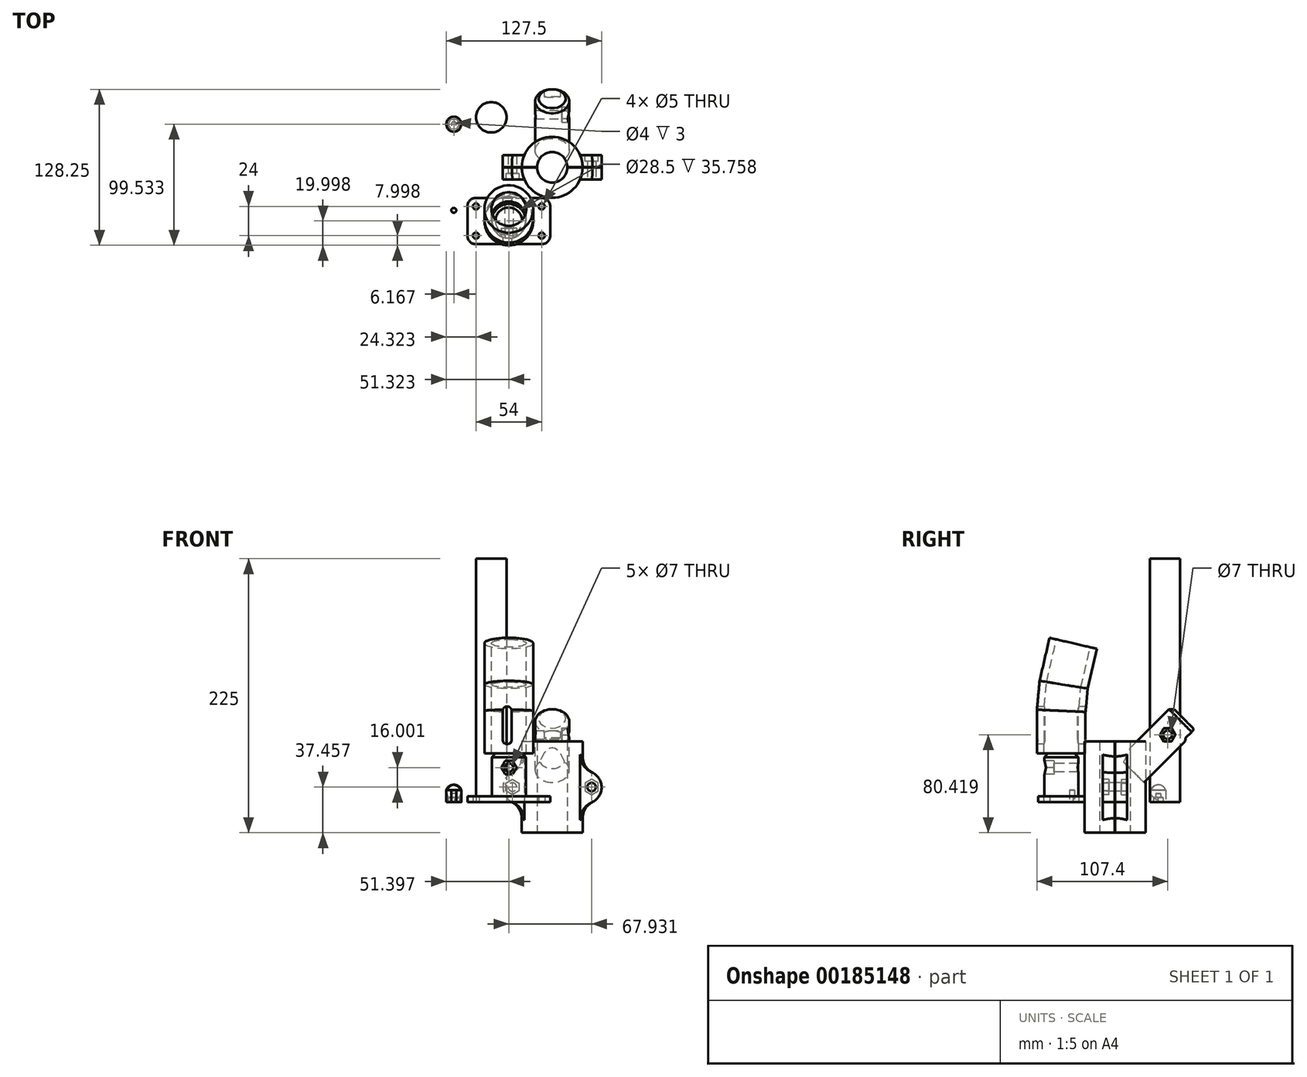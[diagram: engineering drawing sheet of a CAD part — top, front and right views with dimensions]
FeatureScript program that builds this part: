
annotation { "Feature Type Name" : "Feature", "Feature Type Description" : "" }
export const myFeature = defineFeature(function(context is Context, id is Id, definition is map)
    precondition{}
    {
        {
            var Q0;
            Q0=qCreatedBy(makeId("Top.planeOp"),FACE);
            var sketch = newSketch(context, id + "F0", { "sketchPlane" : qUnion([Q0])});
            skCircle(sketch, "E0", {"center": v(0, 0) * mm, "radius": 12.5 * mm});
            skCircle(sketch, "E1", {"center": v(0, 0) * mm, "radius": 25 * mm});
            skSolve(sketch);
        }
        {
            var Q0;
            Q0=makeQuery(id+"F0.imprint","IMPRINT",FACE,{"disambiguationData":[TD([[makeQuery(id+"F0.imprint","IMPRINT",EDGE,{"derivedFrom":sQuery(id+"F0.wireOp",EDGE,"E0")}),-1.0]])]});
            extrude(context, id + "F1", {"entities" : qUnion([Q0]), "depth" : 50 * mm, "symmetric" : true});
        }
        {
            var Q0;
            Q0=qCreatedBy(makeId("Front.planeOp"),FACE);
            var sketch = newSketch(context, id + "F2", { "sketchPlane" : qUnion([Q0])});
            skCircle(sketch, "E2", {"center": v(-26.98, 12.25) * mm, "radius": 13.5 * mm});
            skCircle(sketch, "E3", {"center": v(27.04, 12.25) * mm, "radius": 13.5 * mm});
            skLineSegment(sketch, "E4", {"start": v(27.04, 12.25) * mm, "end": v(-26.98, 12.25) * mm, "construction": true});
            skSolve(sketch);
        }
        {
            var Q0;
            Q0=qSketchRegion(id+"F2",true);
            extrude(context, id + "F3", {"entities" : qUnion([Q0]), "operationType" : NewBodyOperationType.ADD, "depth" : 20 * mm, "symmetric" : true});
        }
        {
            var Q0;
            Q0=makeQuery(id+"F3.opExtrude","CAP_FACE",FACE,{"disambiguationData":[OSD([sQuery(id+"F2.wireOp",EDGE,"E2")])],"isStart":false});
            var sketch = newSketch(context, id + "F4", { "sketchPlane" : qUnion([Q0])});
            skCircle(sketch, "E5", {"center": v(-32.64, 12.46) * mm, "radius": 3.5 * mm});
            skCircle(sketch, "E6", {"center": v(32.37, 12.46) * mm, "radius": 3.5 * mm});
            skLineSegment(sketch, "E7", {"start": v(-40.47, 12.46) * mm, "end": v(40.61, 12.46) * mm, "construction": true});
            skLineSegment(sketch, "E8", {"start": v(32.37, 24.7) * mm, "end": v(32.37, 0) * mm, "construction": true});
            skLineSegment(sketch, "E9", {"start": v(32.37, 0) * mm, "end": v(-32.64, 0) * mm, "construction": true});
            skLineSegment(sketch, "E10", {"start": v(-32.64, 0) * mm, "end": v(-32.64, 24.5) * mm, "construction": true});
            skLineSegment(sketch, "E11", {"start": v(-32.64, 24.5) * mm, "end": v(32.37, 24.7) * mm, "construction": true});
            skSolve(sketch);
        }
        {
            var Q0;
            Q0=qSketchRegion(id+"F4",true);
            extrude(context, id + "F5", {"entities" : qUnion([Q0]), "operationType" : NewBodyOperationType.REMOVE, "oppositeDirection" : true, "depth" : 25 * mm});
        }
        {
            var Q0;
            Q0=makeQuery(id+"F3.opExtrude","CAP_FACE",FACE,{"disambiguationData":[OSD([sQuery(id+"F2.wireOp",EDGE,"E2")])],"isStart":false});
            var sketch = newSketch(context, id + "F6", { "sketchPlane" : qUnion([Q0])});
            skCircle(sketch, "E12.cCircle", {"center": v(-32.64, 12.46) * mm, "radius": 5.5 * mm, "construction": true});
            skLineSegment(sketch, "E12.0", {"start": v(-27.14, 15.63) * mm, "end": v(-27.14, 9.28) * mm});
            skLineSegment(sketch, "E12.1", {"start": v(-27.14, 9.28) * mm, "end": v(-32.64, 6.1) * mm});
            skLineSegment(sketch, "E12.2", {"start": v(-32.64, 6.1) * mm, "end": v(-38.14, 9.28) * mm});
            skLineSegment(sketch, "E12.3", {"start": v(-38.14, 9.28) * mm, "end": v(-38.14, 15.63) * mm});
            skLineSegment(sketch, "E12.4", {"start": v(-38.14, 15.63) * mm, "end": v(-32.64, 18.8) * mm});
            skLineSegment(sketch, "E12.5", {"start": v(-32.64, 18.8) * mm, "end": v(-27.14, 15.63) * mm});
            skPoint(sketch, "E12.0.midPoint", {"position": v(-27.14, 12.46) * mm});
            skLineSegment(sketch, "E13", {"start": v(-38.14, 12.46) * mm, "end": v(-27.14, 12.46) * mm, "construction": true});
            skSolve(sketch);
        }
        {
            var Q0;
            Q0=qSketchRegion(id+"F6",true);
            extrude(context, id + "F7", {"entities" : qUnion([Q0]), "operationType" : NewBodyOperationType.REMOVE, "oppositeDirection" : true, "depth" : 5 * mm});
        }
        {
            var Q0;
            Q0=makeQuery(id+"F3.opExtrude","CAP_FACE",FACE,{"disambiguationData":[OSD([sQuery(id+"F2.wireOp",EDGE,"E3")])],"isStart":true});
            var sketch = newSketch(context, id + "F8", { "sketchPlane" : qUnion([Q0])});
            skCircle(sketch, "E14.cCircle", {"center": v(-32.37, 12.46) * mm, "radius": 5.5 * mm, "construction": true});
            skLineSegment(sketch, "E14.0", {"start": v(-26.87, 15.63) * mm, "end": v(-26.87, 9.28) * mm});
            skLineSegment(sketch, "E14.1", {"start": v(-26.87, 9.28) * mm, "end": v(-32.37, 6.1) * mm});
            skLineSegment(sketch, "E14.2", {"start": v(-32.37, 6.1) * mm, "end": v(-37.87, 9.28) * mm});
            skLineSegment(sketch, "E14.3", {"start": v(-37.87, 9.28) * mm, "end": v(-37.87, 15.63) * mm});
            skLineSegment(sketch, "E14.4", {"start": v(-37.87, 15.63) * mm, "end": v(-32.37, 18.8) * mm});
            skLineSegment(sketch, "E14.5", {"start": v(-32.37, 18.8) * mm, "end": v(-26.87, 15.63) * mm});
            skPoint(sketch, "E14.0.midPoint", {"position": v(-26.87, 12.46) * mm});
            skLineSegment(sketch, "E15", {"start": v(-26.87, 12.46) * mm, "end": v(-37.87, 12.46) * mm, "construction": true});
            skSolve(sketch);
        }
        {
            var Q0;
            Q0=qSketchRegion(id+"F8",true);
            extrude(context, id + "F9", {"entities" : qUnion([Q0]), "operationType" : NewBodyOperationType.REMOVE, "oppositeDirection" : true, "depth" : 5 * mm});
        }
        {
            var Q0;
            {var subQ0=sQuery(id+"F0.wireOp",EDGE,"E0");var subQ1=sQuery(id+"F0.wireOp",EDGE,"E1");Q0=makeQuery(id+"FAVgWfvb4NsKyi1_1.boolean.opBoolean","SPLIT",FACE,{"disambiguationData":[TD([makeQuery(id+"FAVgWfvb4NsKyi1_1.opExtrude","SWEPT_FACE",FACE,{"disambiguationData":[OSD([sQuery(id+"FL5HWG1BF790Trn_1.wireOp",EDGE,"xYHfgR5R-DCME-g4vK-4hEz-Q0mkNuq86y99.top")])]})])],"derivedFrom":makeQuery(id+"F1.opExtrude","CAP_FACE",FACE,{"disambiguationData":[OSD([subQ0,subQ1])],"isStart":false})});}
            extrude(context, id + "F10", {"entities" : qUnion([Q0]), "operationType" : NewBodyOperationType.ADD, "depth" : 25 * mm});
        }
        {
            var Q0;
            Q0=qCreatedBy(makeId("Top.planeOp"),FACE);
            var sketch = newSketch(context, id + "F11", { "sketchPlane" : qUnion([Q0])});
            skLineSegment(sketch, "E16.bottom", {"start": v(-62.64, -25.15) * mm, "end": v(-8.64, -25.15) * mm});
            skLineSegment(sketch, "E16.top", {"start": v(-62.64, -63.15) * mm, "end": v(-8.64, -63.15) * mm});
            skLineSegment(sketch, "E16.left", {"start": v(-69.64, -32.15) * mm, "end": v(-69.64, -56.15) * mm});
            skLineSegment(sketch, "E16.right", {"start": v(-1.64, -32.15) * mm, "end": v(-1.64, -56.15) * mm});
            skCircle(sketch, "E17", {"center": v(-62.64, -32.15) * mm, "radius": 2.5 * mm});
            skCircle(sketch, "E18", {"center": v(-62.64, -56.15) * mm, "radius": 2.5 * mm});
            skCircle(sketch, "E19", {"center": v(-8.64, -32.15) * mm, "radius": 2.5 * mm});
            skCircle(sketch, "E20", {"center": v(-8.64, -56.15) * mm, "radius": 2.5 * mm});
            skLineSegment(sketch, "E21", {"start": v(-62.67, -25.15) * mm, "end": v(-62.64, -32.15) * mm, "construction": true});
            skLineSegment(sketch, "E22", {"start": v(-62.64, -32.15) * mm, "end": v(-69.64, -32.19) * mm, "construction": true});
            skLineSegment(sketch, "E23", {"start": v(-8.64, -56.15) * mm, "end": v(-1.64, -56.15) * mm, "construction": true});
            skLineSegment(sketch, "E24", {"start": v(-8.64, -56.15) * mm, "end": v(-8.64, -63.15) * mm, "construction": true});
            skLineSegment(sketch, "E25.bottom", {"start": v(-62.64, -32.15) * mm, "end": v(-8.64, -32.15) * mm, "construction": true});
            skLineSegment(sketch, "E25.top", {"start": v(-62.64, -56.15) * mm, "end": v(-8.64, -56.15) * mm, "construction": true});
            skLineSegment(sketch, "E25.left", {"start": v(-62.64, -32.15) * mm, "end": v(-62.64, -56.15) * mm, "construction": true});
            skLineSegment(sketch, "E25.right", {"start": v(-8.64, -32.15) * mm, "end": v(-8.64, -56.15) * mm, "construction": true});
            skPoint(sketch, "E26.visualSharp", {"position": v(-69.64, -25.15) * mm});
            skArc(sketch, "E26.filletArc", {"start": v(-62.64, -25.15) * mm, "mid": v(-67.59, -27.2) * mm, "end": v(-69.64, -32.15) * mm});
            skPoint(sketch, "E27.visualSharp", {"position": v(-69.64, -63.15) * mm});
            skArc(sketch, "E27.filletArc", {"start": v(-69.64, -56.15) * mm, "mid": v(-67.59, -61.1) * mm, "end": v(-62.64, -63.15) * mm});
            skPoint(sketch, "E28.visualSharp", {"position": v(-1.64, -63.15) * mm});
            skArc(sketch, "E28.filletArc", {"start": v(-8.64, -63.15) * mm, "mid": v(-3.69, -61.1) * mm, "end": v(-1.64, -56.15) * mm});
            skPoint(sketch, "E29.visualSharp", {"position": v(-1.64, -25.15) * mm});
            skArc(sketch, "E29.filletArc", {"start": v(-1.64, -32.15) * mm, "mid": v(-3.69, -27.2) * mm, "end": v(-8.64, -25.15) * mm});
            skSolve(sketch);
        }
        {
            var Q0;
            Q0=qSketchRegion(id+"F11",true);
            extrude(context, id + "F12", {"entities" : qUnion([Q0]), "depth" : 5 * mm});
        }
        {
            var Q0;
            Q0=makeQuery(id+"F12.opExtrude","CAP_FACE",FACE,{"disambiguationData":[OSD([sQuery(id+"F11.wireOp",EDGE,"E16.bottom"),sQuery(id+"F11.wireOp",EDGE,"E16.top"),sQuery(id+"F11.wireOp",EDGE,"E16.left"),sQuery(id+"F11.wireOp",EDGE,"E16.right"),sQuery(id+"F11.wireOp",EDGE,"E17"),sQuery(id+"F11.wireOp",EDGE,"E18"),sQuery(id+"F11.wireOp",EDGE,"E19"),sQuery(id+"F11.wireOp",EDGE,"E20"),sQuery(id+"F11.wireOp",EDGE,"E26.filletArc"),sQuery(id+"F11.wireOp",EDGE,"E27.filletArc"),sQuery(id+"F11.wireOp",EDGE,"E28.filletArc"),sQuery(id+"F11.wireOp",EDGE,"E29.filletArc")])],"isStart":false});
            var sketch = newSketch(context, id + "F13", { "sketchPlane" : qUnion([Q0])});
            skCircle(sketch, "E30", {"center": v(-35.64, -44.15) * mm, "radius": 14 * mm});
            skLineSegment(sketch, "E31", {"start": v(-69.64, -44.15) * mm, "end": v(-1.64, -44.15) * mm, "construction": true});
            skLineSegment(sketch, "E32", {"start": v(-35.64, -25.15) * mm, "end": v(-35.64, -63.15) * mm, "construction": true});
            skSolve(sketch);
        }
        {
            var Q0;
            Q0=qSketchRegion(id+"F13",true);
            extrude(context, id + "F14", {"entities" : qUnion([Q0]), "operationType" : NewBodyOperationType.ADD, "depth" : 35 * mm});
        }
        {
            var Q0;
            Q0=qCreatedBy(makeId("Top.planeOp"),FACE);
            var sketch = newSketch(context, id + "F15", { "sketchPlane" : qUnion([Q0])});
            skCircle(sketch, "E33", {"center": v(-50.03, 41.05) * mm, "radius": 12.5 * mm});
            skSolve(sketch);
        }
        {
            var Q0;
            Q0=qSketchRegion(id+"F15",true);
            extrude(context, id + "F16", {"entities" : qUnion([Q0]), "depth" : 200 * mm});
        }
        {
            var Q0;
            Q0=makeQuery(id+"F14.opExtrude","CAP_FACE",FACE,{"disambiguationData":[OSD([sQuery(id+"F13.wireOp",EDGE,"E30")])],"isStart":false});
            var sketch = newSketch(context, id + "F17", { "sketchPlane" : qUnion([Q0])});
            skCircle(sketch, "E34", {"center": v(-35.64, -44.15) * mm, "radius": 14.25 * mm});
            skCircle(sketch, "E35", {"center": v(-35.64, -44.15) * mm, "radius": 20 * mm});
            skSolve(sketch);
        }
        {
            var Q0;
            Q0=qCreatedBy(makeId("Right.planeOp"),FACE);
            cPlane(context, id + "F18", {"entities" : qUnion([Q0]), "cplaneType" : CPlaneType.OFFSET, "offset" : 37 * mm, "oppositeDirection" : true, "width" : 150 * mm, "height" : 150 * mm});
        }
        {
            var Q0;
            Q0=qCreatedBy(id+"F18.planeOp",FACE);
            var sketch = newSketch(context, id + "F19", { "sketchPlane" : qUnion([Q0])});
            skLineSegment(sketch, "E36", {"start": v(-44.05, 40.1) * mm, "end": v(-44.05, 75.1) * mm});
            skLineSegment(sketch, "E37", {"start": v(-57.92, 40.1) * mm, "end": v(-30.17, 40.1) * mm, "construction": true});
            skLineSegment(sketch, "E38", {"start": v(-42.05, 96.55) * mm, "end": v(-34.15, 130.64) * mm});
            skLineSegment(sketch, "E39", {"start": v(-42.05, 96.55) * mm, "end": v(-44.05, 75.1) * mm});
            skSolve(sketch);
        }
        {
            var Q0;
            Q0=makeQuery(id+"F17.imprint","IMPRINT",FACE,{"disambiguationData":[TD([[makeQuery(id+"F17.imprint","IMPRINT",EDGE,{"derivedFrom":sQuery(id+"F17.wireOp",EDGE,"E34")}),-1.0]])]});
            var Q1;
            Q1=sQuery(id+"F19.wireOp",EDGE,"E36");
            var Q2;
            Q2=sQuery(id+"F19.wireOp",EDGE,"E39");
            var Q3;
            Q3=sQuery(id+"F19.wireOp",EDGE,"E38");
            sweep(context, id + "F20", {"profiles" : qUnion([Q0]), "path" : qUnion([Q1, Q2, Q3])});
        }
        {
            var Q0;
            Q0=makeQuery(id+"F12.opExtrude","CAP_FACE",FACE,{"disambiguationData":[OSD([sQuery(id+"F11.wireOp",EDGE,"E16.bottom"),sQuery(id+"F11.wireOp",EDGE,"E16.top"),sQuery(id+"F11.wireOp",EDGE,"E16.left"),sQuery(id+"F11.wireOp",EDGE,"E16.right"),sQuery(id+"F11.wireOp",EDGE,"E17"),sQuery(id+"F11.wireOp",EDGE,"E18"),sQuery(id+"F11.wireOp",EDGE,"E19"),sQuery(id+"F11.wireOp",EDGE,"E20"),sQuery(id+"F11.wireOp",EDGE,"E26.filletArc"),sQuery(id+"F11.wireOp",EDGE,"E27.filletArc"),sQuery(id+"F11.wireOp",EDGE,"E28.filletArc"),sQuery(id+"F11.wireOp",EDGE,"E29.filletArc")])],"isStart":true});
            var sketch = newSketch(context, id + "F21", { "sketchPlane" : qUnion([Q0])});
            skCircle(sketch, "E40", {"center": v(-62.64, 56.15) * mm, "radius": 2.5 * mm});
            skCircle(sketch, "E41", {"center": v(-62.64, 56.15) * mm, "radius": 5.5 * mm});
            skSolve(sketch);
        }
        {
            var Q0;
            Q0=makeQuery(id+"F21.imprint","IMPRINT",FACE,{"disambiguationData":[TD([[makeQuery(id+"F21.imprint","IMPRINT",EDGE,{"derivedFrom":sQuery(id+"F21.wireOp",EDGE,"E40")}),-1.0]])]});
            extrude(context, id + "F22", {"entities" : qUnion([Q0]), "depth" : 2.5 * mm});
        }
        {
            var Q0;
            Q0=qCreatedBy(makeId("Top.planeOp"),FACE);
            var sketch = newSketch(context, id + "F23", { "sketchPlane" : qUnion([Q0])});
            skCircle(sketch, "E42", {"center": v(0, 56.93) * mm, "radius": 14 * mm});
            skSolve(sketch);
        }
        {
            var Q0;
            Q0=qSketchRegion(id+"F23",true);
            extrude(context, id + "F24", {"entities" : qUnion([Q0]), "depth" : 50 * mm});
        }
        {
            var Q0;
            Q0=makeQuery(id+"F24.opExtrude","SWEPT_BODY",BODY,{"disambiguationData":[OSD([sQuery(id+"F23.wireOp",EDGE,"E42")])]});
            var Q1;
            Q1=makeQuery(id+"F24.opExtrude","CAP_EDGE",EDGE,{"disambiguationData":[OSD([sQuery(id+"F23.wireOp",EDGE,"E42")])],"isStart":true});
            transform(context, id + "F25", {"entities" : qUnion([Q0]), "transformType" : TransformType.ROTATION, "transformAxis" : qUnion([Q1]), "angle" : 30 * degree, "makeCopy" : false});
        }
        {
            var Q0;
            Q0=qCreatedBy(makeId("Right.planeOp"),FACE);
            var sketch = newSketch(context, id + "F26", { "sketchPlane" : qUnion([Q0])});
            skLineSegment(sketch, "E43", {"start": v(46.27, -2.3) * mm, "end": v(41.48, 4.24) * mm});
            skLineSegment(sketch, "E44", {"start": v(41.48, 4.24) * mm, "end": v(41.48, -4.7) * mm});
            skLineSegment(sketch, "E45", {"start": v(41.48, -4.7) * mm, "end": v(46.27, -2.3) * mm});
            skSolve(sketch);
        }
        {
            var Q0;
            Q0=qSketchRegion(id+"F26",true);
            extrude(context, id + "F27", {"entities" : qUnion([Q0]), "operationType" : NewBodyOperationType.REMOVE, "oppositeDirection" : true, "depth" : 25 * mm, "symmetric" : true});
        }
        {
            var Q0;
            Q0=makeQuery(id+"F24.opExtrude","SWEPT_BODY",BODY,{"disambiguationData":[OSD([sQuery(id+"F23.wireOp",EDGE,"E42")])]});
            var Q1;
            Q1=makeQuery(id+"F27.boolean.opBoolean","INTERSECT",EDGE,{"derivedFrom":[makeQuery(id+"F24.opExtrude","CAP_FACE",FACE,{"disambiguationData":[OSD([sQuery(id+"F23.wireOp",EDGE,"E42")])],"isStart":true}),makeQuery(id+"F27.opExtrude","SWEPT_FACE",FACE,{"disambiguationData":[OSD([sQuery(id+"F26.wireOp",EDGE,"E43")])]})]});
            transform(context, id + "F28", {"entities" : qUnion([Q0]), "transformType" : TransformType.ROTATION, "transformAxis" : qUnion([Q1]), "angle" : 225 * degree, "makeCopy" : false});
        }
        {
            var Q0;
            Q0=makeQuery(id+"F24.opExtrude","SWEPT_BODY",BODY,{"disambiguationData":[OSD([sQuery(id+"F23.wireOp",EDGE,"E42")])]});
            transform(context, id + "F29", {"entities" : qUnion([Q0]), "transformType" : TransformType.TRANSLATION_3D, "dx" : 0 * mm, "dy" : 13.4 * mm, "dz" : 52.8 * mm, "makeCopy" : false});
        }
        {
            var Q0;
            Q0=makeQuery(id+"F24.opExtrude","CAP_FACE",FACE,{"disambiguationData":[OSD([sQuery(id+"F23.wireOp",EDGE,"E42")])],"isStart":true});
            extrude(context, id + "F30", {"entities" : qUnion([Q0]), "operationType" : NewBodyOperationType.ADD, "depth" : 10 * mm});
        }
        {
            var Q0;
            Q0=qCreatedBy(makeId("Front.planeOp"),FACE);
            cPlane(context, id + "F31", {"entities" : qUnion([Q0]), "cplaneType" : CPlaneType.OFFSET, "offset" : 60 * mm, "width" : 150 * mm, "height" : 150 * mm});
        }
        {
            var Q0;
            Q0=qCreatedBy(id+"F31.planeOp",FACE);
            var sketch = newSketch(context, id + "F32", { "sketchPlane" : qUnion([Q0])});
            skCircle(sketch, "E46.cCircle", {"center": v(-35.54, 28.49) * mm, "radius": 5.5 * mm, "construction": true});
            skLineSegment(sketch, "E46.0", {"start": v(-32.36, 22.99) * mm, "end": v(-38.71, 22.99) * mm});
            skLineSegment(sketch, "E46.1", {"start": v(-38.71, 22.99) * mm, "end": v(-41.89, 28.49) * mm});
            skLineSegment(sketch, "E46.2", {"start": v(-41.89, 28.49) * mm, "end": v(-38.71, 33.99) * mm});
            skLineSegment(sketch, "E46.3", {"start": v(-38.71, 33.99) * mm, "end": v(-32.36, 33.99) * mm});
            skLineSegment(sketch, "E46.4", {"start": v(-32.36, 33.99) * mm, "end": v(-29.19, 28.49) * mm});
            skLineSegment(sketch, "E46.5", {"start": v(-29.19, 28.49) * mm, "end": v(-32.36, 22.99) * mm});
            skPoint(sketch, "E46.0.midPoint", {"position": v(-35.54, 22.99) * mm});
            skLineSegment(sketch, "E47", {"start": v(-35.54, 33.99) * mm, "end": v(-35.54, 22.99) * mm, "construction": true});
            skSolve(sketch);
        }
        {
            var Q0;
            Q0=qSketchRegion(id+"F32",true);
            extrude(context, id + "F33", {"entities" : qUnion([Q0]), "operationType" : NewBodyOperationType.REMOVE, "oppositeDirection" : true, "depth" : 10 * mm});
        }
        {
            var Q0;
            Q0=qCreatedBy(id+"F31.planeOp",FACE);
            var sketch = newSketch(context, id + "F34", { "sketchPlane" : qUnion([Q0])});
            skCircle(sketch, "E48", {"center": v(-35.56, 28.46) * mm, "radius": 3.5 * mm});
            skLineSegment(sketch, "E49", {"start": v(-35.56, 33.8) * mm, "end": v(-35.56, 23.2) * mm, "construction": true});
            skLineSegment(sketch, "E50", {"start": v(-35.56, 23.2) * mm, "end": v(-35.56, 23.2) * mm});
            skLineSegment(sketch, "E51", {"start": v(-29.46, 28.46) * mm, "end": v(-41.66, 28.46) * mm, "construction": true});
            skSolve(sketch);
        }
        {
            var Q0;
            Q0=qSketchRegion(id+"F34",true);
            extrude(context, id + "F35", {"entities" : qUnion([Q0]), "operationType" : NewBodyOperationType.REMOVE, "oppositeDirection" : true, "depth" : 50 * mm});
        }
        {
            var Q0;
            Q0=qCreatedBy(id+"F31.planeOp",FACE);
            var sketch = newSketch(context, id + "F36", { "sketchPlane" : qUnion([Q0])});
            skLineSegment(sketch, "E52", {"start": v(-36.97, 51.53) * mm, "end": v(-36.97, 74.9) * mm});
            skArc(sketch, "E53.0.startCap", {"start": v(-33.22, 51.53) * mm, "mid": v(-36.97, 47.78) * mm, "end": v(-40.72, 51.53) * mm});
            skArc(sketch, "E53.0.endCap", {"start": v(-40.72, 74.9) * mm, "mid": v(-36.97, 78.65) * mm, "end": v(-33.22, 74.9) * mm});
            skLineSegment(sketch, "E53.0.left", {"start": v(-40.72, 51.53) * mm, "end": v(-40.72, 74.9) * mm});
            skLineSegment(sketch, "E53.0.right", {"start": v(-33.22, 51.53) * mm, "end": v(-33.22, 74.9) * mm});
            skSolve(sketch);
        }
        {
            var Q0;
            Q0=qSketchRegion(id+"F36",true);
            extrude(context, id + "F37", {"entities" : qUnion([Q0]), "operationType" : NewBodyOperationType.REMOVE, "oppositeDirection" : true, "depth" : 81.2 * mm, "symmetric" : true});
        }
        {
            var Q0;
            Q0=makeQuery(id+"F30.opExtrude","CAP_EDGE",EDGE,{"disambiguationData":[OSD([sQuery(id+"F23.wireOp",EDGE,"E42")])],"isStart":false});
            chamfer(context, id + "F38", {"entities" : qUnion([Q0]), "width" : 3 * mm, "tangentPropagation" : true});
        }
        {
            var Q0;
            Q0=makeQuery(id+"F14.opExtrude","CAP_EDGE",EDGE,{"disambiguationData":[OSD([sQuery(id+"F13.wireOp",EDGE,"E30")])],"isStart":false});
            chamfer(context, id + "F39", {"entities" : qUnion([Q0]), "width" : 3 * mm, "tangentPropagation" : true});
        }
        {
            var Q0;
            Q0=qCreatedBy(makeId("Right.planeOp"),FACE);
            cPlane(context, id + "F40", {"entities" : qUnion([Q0]), "cplaneType" : CPlaneType.OFFSET, "offset" : 15 * mm, "width" : 150 * mm, "height" : 150 * mm});
        }
        {
            var Q0;
            Q0=qCreatedBy(id+"F40.planeOp",FACE);
            var sketch = newSketch(context, id + "F41", { "sketchPlane" : qUnion([Q0])});
            skCircle(sketch, "E54.cCircle", {"center": v(43.25, 55.42) * mm, "radius": 5.5 * mm, "construction": true});
            skLineSegment(sketch, "E54.0", {"start": v(49.6, 55.48) * mm, "end": v(46.48, 49.95) * mm});
            skLineSegment(sketch, "E54.1", {"start": v(46.48, 49.95) * mm, "end": v(40.12, 49.89) * mm});
            skLineSegment(sketch, "E54.2", {"start": v(40.12, 49.89) * mm, "end": v(36.9, 55.36) * mm});
            skLineSegment(sketch, "E54.3", {"start": v(36.9, 55.36) * mm, "end": v(40.02, 60.89) * mm});
            skLineSegment(sketch, "E54.4", {"start": v(40.02, 60.89) * mm, "end": v(46.37, 60.95) * mm});
            skLineSegment(sketch, "E54.5", {"start": v(46.37, 60.95) * mm, "end": v(49.6, 55.48) * mm});
            skPoint(sketch, "E54.0.midPoint", {"position": v(48.04, 52.71) * mm});
            skLineSegment(sketch, "E55", {"start": v(43.25, 60.92) * mm, "end": v(43.3, 49.92) * mm, "construction": true});
            skLineSegment(sketch, "E56", {"start": v(57.63, 50.13) * mm, "end": v(37.54, 69.64) * mm, "construction": true});
            skLineSegment(sketch, "E57", {"start": v(47.59, 59.88) * mm, "end": v(31.55, 43.38) * mm, "construction": true});
            skSolve(sketch);
        }
        {
            var Q0;
            Q0=makeQuery(id+"F41.imprint","IMPRINT",FACE,{"disambiguationData":[TD([[makeQuery(id+"F41.imprint","IMPRINT",EDGE,{"derivedFrom":sQuery(id+"F41.wireOp",EDGE,"E54.0")}),-1.0]])]});
            extrude(context, id + "F42", {"entities" : qUnion([Q0]), "operationType" : NewBodyOperationType.REMOVE, "oppositeDirection" : true, "depth" : 7 * mm});
        }
        {
            var Q0;
            Q0=makeQuery(id+"F42.boolean.opBoolean","COPY",FACE,{"derivedFrom":makeQuery(id+"F42.opExtrude","CAP_FACE",FACE,{"disambiguationData":[OSD([sQuery(id+"F41.wireOp",EDGE,"E54.0"),sQuery(id+"F41.wireOp",EDGE,"E54.1"),sQuery(id+"F41.wireOp",EDGE,"E54.2"),sQuery(id+"F41.wireOp",EDGE,"E54.3"),sQuery(id+"F41.wireOp",EDGE,"E54.4"),sQuery(id+"F41.wireOp",EDGE,"E54.5")])],"isStart":false})});
            var sketch = newSketch(context, id + "F43", { "sketchPlane" : qUnion([Q0])});
            skCircle(sketch, "E58", {"center": v(43.25, 55.42) * mm, "radius": 3.5 * mm});
            skLineSegment(sketch, "E59", {"start": v(40.02, 60.89) * mm, "end": v(46.48, 49.95) * mm, "construction": true});
            skLineSegment(sketch, "E60", {"start": v(46.37, 60.95) * mm, "end": v(40.12, 49.89) * mm, "construction": true});
            skSolve(sketch);
        }
        {
            var Q0;
            Q0=qSketchRegion(id+"F43",true);
            extrude(context, id + "F44", {"entities" : qUnion([Q0]), "operationType" : NewBodyOperationType.REMOVE, "oppositeDirection" : true, "depth" : 25 * mm});
        }
        {
            var Q0;
            Q0=makeQuery(id+"F10.opExtrude","CAP_FACE",FACE,{"disambiguationData":[OSD([sQuery(id+"F0.wireOp",EDGE,"E0"),sQuery(id+"F0.wireOp",EDGE,"E1")])],"isStart":false});
            var sketch = newSketch(context, id + "F45", { "sketchPlane" : qUnion([Q0])});
            skLineSegment(sketch, "E61.bottom", {"start": v(-22.91, 10) * mm, "end": v(-22.22, 10) * mm});
            skLineSegment(sketch, "E61.top", {"start": v(-22.91, -10) * mm, "end": v(-22.22, -10) * mm});
            skLineSegment(sketch, "E61.right", {"start": v(-22.22, 10) * mm, "end": v(-22.22, -10) * mm});
            skLineSegment(sketch, "E62.bottom", {"start": v(22.92, 10) * mm, "end": v(22.1, 10) * mm});
            skLineSegment(sketch, "E62.top", {"start": v(22.91, -10) * mm, "end": v(22.1, -10) * mm});
            skLineSegment(sketch, "E62.right", {"start": v(22.1, 10) * mm, "end": v(22.1, -10) * mm});
            skArc(sketch, "E63", {"start": v(22.91, -10) * mm, "mid": v(25, 0) * mm, "end": v(22.92, 10) * mm});
            skArc(sketch, "E64.trimOffspring", {"start": v(-22.91, 10) * mm, "mid": v(-25, 0) * mm, "end": v(-22.91, -10) * mm});
            skSolve(sketch);
        }
        {
            var Q0;
            {var subQ1=sQuery(id+"F2.wireOp",EDGE,"E2");var subQ2=sQuery(id+"F0.wireOp",EDGE,"E1");var subQ3=sQuery(id+"F0.wireOp",EDGE,"E0");var subQ4=makeQuery(id+"F1.opExtrude","CAP_FACE",FACE,{"disambiguationData":[OSD([subQ3,subQ2])],"isStart":false});var subQ8=makeQuery(id+"F3.opExtrude","CAP_FACE",FACE,{"disambiguationData":[OSD([subQ1])],"isStart":false});var subQ15=makeQuery(id+"F10.opExtrude","CAP_EDGE",EDGE,{"disambiguationData":[OSD([subQ3,subQ2,subQ1]),TDD([makeQuery(id+"F3.boolean.opBoolean","INTERSECT",EDGE,{"derivedFrom":[subQ4,subQ8]})])],"isStart":false});Q0=makeQuery(id+"F45.imprint","IMPRINT",FACE,{"disambiguationData":[TD([[makeQuery(id+"F45.imprint","IMPRINT",EDGE,{"derivedFrom":subQ15}),1.0]])]});}
            var Q1;
            {var subQ1=sQuery(id+"F2.wireOp",EDGE,"E3");var subQ2=sQuery(id+"F0.wireOp",EDGE,"E1");var subQ3=sQuery(id+"F0.wireOp",EDGE,"E0");var subQ4=makeQuery(id+"F1.opExtrude","CAP_FACE",FACE,{"disambiguationData":[OSD([subQ3,subQ2])],"isStart":false});var subQ5=makeQuery(id+"F10.opExtrude","CAP_EDGE",EDGE,{"disambiguationData":[OSD([subQ3,subQ2,subQ1]),TDD([makeQuery(id+"F3.boolean.opBoolean","INTERSECT",EDGE,{"derivedFrom":[subQ4,makeQuery(id+"F3.opExtrude","SWEPT_FACE",FACE,{"disambiguationData":[OSD([subQ1])]})]})])],"isStart":false});Q1=makeQuery(id+"F45.imprint","IMPRINT",FACE,{"disambiguationData":[TD([[makeQuery(id+"F45.imprint","IMPRINT",EDGE,{"derivedFrom":subQ5}),-1.0]])]});}
            extrude(context, id + "F46", {"entities" : qUnion([Q0, Q1]), "operationType" : NewBodyOperationType.ADD, "oppositeDirection" : true, "depth" : 25 * mm});
        }
        {
            var Q0;
            {var subQ0=sQuery(id+"F0.wireOp",EDGE,"E1");var subQ1=sQuery(id+"F0.wireOp",EDGE,"E0");Q0=makeQuery(id+"F46.boolean.opBoolean","MERGE",FACE,{"derivedFrom":[makeQuery(id+"F10.opExtrude","CAP_FACE",FACE,{"disambiguationData":[OSD([subQ1,subQ0])],"isStart":false}),makeQuery(id+"F46.opExtrude","CAP_FACE",FACE,{"disambiguationData":[OSD([subQ1,subQ0,sQuery(id+"F2.wireOp",EDGE,"E2"),sQuery(id+"F45.wireOp",EDGE,"E61.bottom"),sQuery(id+"F45.wireOp",EDGE,"E61.left")])],"isStart":true}),makeQuery(id+"F46.opExtrude","CAP_FACE",FACE,{"disambiguationData":[OSD([subQ1,subQ0,sQuery(id+"F2.wireOp",EDGE,"E3"),sQuery(id+"F45.wireOp",EDGE,"E62.bottom"),sQuery(id+"F45.wireOp",EDGE,"E62.left")])],"isStart":true})]});}
            var sketch = newSketch(context, id + "F47", { "sketchPlane" : qUnion([Q0])});
            skLineSegment(sketch, "E65.bottom", {"start": v(-40.89, 0.2) * mm, "end": v(42.17, 0.2) * mm});
            skLineSegment(sketch, "E65.top", {"start": v(-40.89, -0.2) * mm, "end": v(42.17, -0.2) * mm});
            skLineSegment(sketch, "E65.left", {"start": v(-40.89, 0.2) * mm, "end": v(-40.89, -0.2) * mm});
            skLineSegment(sketch, "E65.right", {"start": v(42.17, 0.2) * mm, "end": v(42.17, -0.2) * mm});
            skPoint(sketch, "E65.middle", {"position": v(0.64, 0) * mm});
            skLineSegment(sketch, "E66", {"start": v(0, -12.5) * mm, "end": v(0, 12.5) * mm, "construction": true});
            skLineSegment(sketch, "E67", {"start": v(0, 0) * mm, "end": v(0.04, 0) * mm, "construction": true});
            skPoint(sketch, "E67.endSnap0", {"position": v(0, 0) * mm});
            skLineSegment(sketch, "E68", {"start": v(0, 0) * mm, "end": v(0, 0.2) * mm, "construction": true});
            skSolve(sketch);
        }
        {
            var Q0;
            {var subQ0=sQuery(id+"F47.wireOp",EDGE,"E65.bottom");var subQ1=makeQuery(id+"F46.opExtrude","CAP_EDGE",EDGE,{"disambiguationData":[OSD([sQuery(id+"F45.wireOp",EDGE,"E61.left")])],"isStart":true});var subQ2=makeQuery(id+"F47.imprint","INTERSECT",VERTEX,{"derivedFrom":[subQ1,subQ0]});Q0=makeQuery(id+"F47.imprint","IMPRINT",FACE,{"disambiguationData":[TD([[makeQuery(id+"F47.imprint","IMPRINT",EDGE,{"disambiguationData":[TD([[subQ2,-1.0]])],"derivedFrom":subQ0}),-1.0]])]});}
            var Q1;
            {var subQ0=sQuery(id+"F47.wireOp",EDGE,"E65.left");Q1=makeQuery(id+"F47.imprint","IMPRINT",FACE,{"disambiguationData":[TD([[makeQuery(id+"F47.imprint","IMPRINT",EDGE,{"derivedFrom":subQ0}),1.0]])]});}
            var Q2;
            {var subQ0=sQuery(id+"F47.wireOp",EDGE,"E65.bottom");var subQ1=makeQuery(id+"F46.opExtrude","CAP_EDGE",EDGE,{"disambiguationData":[OSD([sQuery(id+"F45.wireOp",EDGE,"E62.left")])],"isStart":true});var subQ2=makeQuery(id+"F47.imprint","INTERSECT",VERTEX,{"derivedFrom":[subQ1,subQ0]});Q2=makeQuery(id+"F47.imprint","IMPRINT",FACE,{"disambiguationData":[TD([[makeQuery(id+"F47.imprint","IMPRINT",EDGE,{"disambiguationData":[TD([[subQ2,1.0]])],"derivedFrom":subQ0}),-1.0]])]});}
            var Q3;
            {var subQ0=sQuery(id+"F47.wireOp",EDGE,"E65.right");Q3=makeQuery(id+"F47.imprint","IMPRINT",FACE,{"disambiguationData":[TD([[makeQuery(id+"F47.imprint","IMPRINT",EDGE,{"derivedFrom":subQ0}),-1.0]])]});}
            extrude(context, id + "F48", {"entities" : qUnion([Q0, Q1, Q2, Q3]), "operationType" : NewBodyOperationType.REMOVE, "oppositeDirection" : true, "depth" : 200 * mm});
        }
        {
            var Q0;
            Q0=qCreatedBy(makeId("Top.planeOp"),FACE);
            var sketch = newSketch(context, id + "F49", { "sketchPlane" : qUnion([Q0])});
            skCircle(sketch, "E69", {"center": v(0, 0) * mm, "radius": 12.5 * mm});
            skSolve(sketch);
        }
        {
            var Q0;
            Q0=qSketchRegion(id+"F49",true);
            extrude(context, id + "F50", {"entities" : qUnion([Q0]), "operationType" : NewBodyOperationType.REMOVE, "depth" : 93 * mm, "symmetric" : true});
        }
        {
            var Q0;
            Q0=makeQuery(id+"F22.opExtrude","SWEPT_BODY",BODY,{"disambiguationData":[OSD([sQuery(id+"F21.wireOp",EDGE,"E40"),sQuery(id+"F21.wireOp",EDGE,"E41")])]});
            deleteBodies(context, id + "F51", {"entities" : qUnion([Q0])});
        }
        {
            var Q0;
            {var subQ0=sQuery(id+"F0.wireOp",EDGE,"E1");var subQ2=makeQuery(id+"F1.opExtrude","SWEPT_FACE",FACE,{"disambiguationData":[OSD([subQ0])]});var subQ3=sQuery(id+"F2.wireOp",EDGE,"E2");var subQ6=makeQuery(id+"F3.opExtrude","CAP_FACE",FACE,{"disambiguationData":[OSD([subQ3])],"isStart":false});var subQ7=makeQuery(id+"F3.opExtrude","SWEPT_FACE",FACE,{"disambiguationData":[OSD([subQ3])]});Q0=makeQuery(id+"F48.boolean.opBoolean","SPLIT",EDGE,{"disambiguationData":[TD([subQ6])],"derivedFrom":makeQuery(id+"F3.boolean.opBoolean","INTERSECT",EDGE,{"derivedFrom":[subQ2,subQ7]})});}
            var Q1;
            {var subQ0=sQuery(id+"F0.wireOp",EDGE,"E1");var subQ2=makeQuery(id+"F1.opExtrude","SWEPT_FACE",FACE,{"disambiguationData":[OSD([subQ0])]});var subQ3=sQuery(id+"F2.wireOp",EDGE,"E2");var subQ4=makeQuery(id+"F3.opExtrude","CAP_FACE",FACE,{"disambiguationData":[OSD([subQ3])],"isStart":true});var subQ7=makeQuery(id+"F3.opExtrude","SWEPT_FACE",FACE,{"disambiguationData":[OSD([subQ3])]});Q1=makeQuery(id+"F48.boolean.opBoolean","SPLIT",EDGE,{"disambiguationData":[TD([subQ4])],"derivedFrom":makeQuery(id+"F3.boolean.opBoolean","INTERSECT",EDGE,{"derivedFrom":[subQ2,subQ7]})});}
            var Q2;
            {var subQ0=sQuery(id+"F0.wireOp",EDGE,"E1");var subQ2=makeQuery(id+"F1.opExtrude","SWEPT_FACE",FACE,{"disambiguationData":[OSD([subQ0])]});var subQ4=sQuery(id+"F2.wireOp",EDGE,"E3");var subQ6=makeQuery(id+"F3.opExtrude","CAP_FACE",FACE,{"disambiguationData":[OSD([subQ4])],"isStart":false});var subQ7=makeQuery(id+"F3.opExtrude","SWEPT_FACE",FACE,{"disambiguationData":[OSD([subQ4])]});Q2=makeQuery(id+"F48.boolean.opBoolean","SPLIT",EDGE,{"disambiguationData":[TD([subQ6])],"derivedFrom":makeQuery(id+"F3.boolean.opBoolean","INTERSECT",EDGE,{"derivedFrom":[subQ2,subQ7]})});}
            var Q3;
            {var subQ0=sQuery(id+"F0.wireOp",EDGE,"E1");var subQ2=makeQuery(id+"F1.opExtrude","SWEPT_FACE",FACE,{"disambiguationData":[OSD([subQ0])]});var subQ4=sQuery(id+"F2.wireOp",EDGE,"E3");var subQ5=makeQuery(id+"F3.opExtrude","CAP_FACE",FACE,{"disambiguationData":[OSD([subQ4])],"isStart":true});var subQ7=makeQuery(id+"F3.opExtrude","SWEPT_FACE",FACE,{"disambiguationData":[OSD([subQ4])]});Q3=makeQuery(id+"F48.boolean.opBoolean","SPLIT",EDGE,{"disambiguationData":[TD([subQ5])],"derivedFrom":makeQuery(id+"F3.boolean.opBoolean","INTERSECT",EDGE,{"derivedFrom":[subQ2,subQ7]})});}
            var Q4;
            {var subQ4=sQuery(id+"F2.wireOp",EDGE,"E3");var subQ6=makeQuery(id+"F3.opExtrude","CAP_FACE",FACE,{"disambiguationData":[OSD([subQ4])],"isStart":false});var subQ7=makeQuery(id+"F3.opExtrude","SWEPT_FACE",FACE,{"disambiguationData":[OSD([subQ4])]});var subQ8=makeQuery(id+"F46.opExtrude","SWEPT_FACE",FACE,{"disambiguationData":[OSD([sQuery(id+"F45.wireOp",EDGE,"E63")])]});Q4=makeQuery(id+"F48.boolean.opBoolean","SPLIT",EDGE,{"disambiguationData":[TD([subQ6])],"derivedFrom":makeQuery(id+"F46.boolean.opBoolean","INTERSECT",EDGE,{"derivedFrom":[subQ7,subQ8]})});}
            var Q5;
            {var subQ4=sQuery(id+"F2.wireOp",EDGE,"E3");var subQ5=makeQuery(id+"F3.opExtrude","CAP_FACE",FACE,{"disambiguationData":[OSD([subQ4])],"isStart":true});var subQ7=makeQuery(id+"F3.opExtrude","SWEPT_FACE",FACE,{"disambiguationData":[OSD([subQ4])]});var subQ8=makeQuery(id+"F46.opExtrude","SWEPT_FACE",FACE,{"disambiguationData":[OSD([sQuery(id+"F45.wireOp",EDGE,"E63")])]});Q5=makeQuery(id+"F48.boolean.opBoolean","SPLIT",EDGE,{"disambiguationData":[TD([subQ5])],"derivedFrom":makeQuery(id+"F46.boolean.opBoolean","INTERSECT",EDGE,{"derivedFrom":[subQ7,subQ8]})});}
            var Q6;
            {var subQ3=sQuery(id+"F2.wireOp",EDGE,"E2");var subQ6=makeQuery(id+"F3.opExtrude","CAP_FACE",FACE,{"disambiguationData":[OSD([subQ3])],"isStart":false});var subQ7=makeQuery(id+"F3.opExtrude","SWEPT_FACE",FACE,{"disambiguationData":[OSD([subQ3])]});var subQ8=makeQuery(id+"F46.opExtrude","SWEPT_FACE",FACE,{"disambiguationData":[OSD([sQuery(id+"F45.wireOp",EDGE,"E64.trimOffspring")])]});Q6=makeQuery(id+"F48.boolean.opBoolean","SPLIT",EDGE,{"disambiguationData":[TD([subQ6])],"derivedFrom":makeQuery(id+"F46.boolean.opBoolean","INTERSECT",EDGE,{"derivedFrom":[subQ7,subQ8]})});}
            var Q7;
            {var subQ3=sQuery(id+"F2.wireOp",EDGE,"E2");var subQ4=makeQuery(id+"F3.opExtrude","CAP_FACE",FACE,{"disambiguationData":[OSD([subQ3])],"isStart":true});var subQ7=makeQuery(id+"F46.opExtrude","SWEPT_FACE",FACE,{"disambiguationData":[OSD([sQuery(id+"F45.wireOp",EDGE,"E64.trimOffspring")])]});var subQ8=makeQuery(id+"F3.opExtrude","SWEPT_FACE",FACE,{"disambiguationData":[OSD([subQ3])]});Q7=makeQuery(id+"F48.boolean.opBoolean","SPLIT",EDGE,{"disambiguationData":[TD([subQ4])],"derivedFrom":makeQuery(id+"F46.boolean.opBoolean","INTERSECT",EDGE,{"derivedFrom":[subQ8,subQ7]})});}
            fillet(context, id + "F52", {"entities" : qUnion([Q0, Q1, Q2, Q3, Q4, Q5, Q6, Q7]), "radius" : 15 * mm, "tangentPropagation" : true, "allowEdgeOverflow" : false});
        }
        {
            var Q0;
            Q0=qCreatedBy(makeId("Top.planeOp"),FACE);
            var sketch = newSketch(context, id + "F53", { "sketchPlane" : qUnion([Q0])});
            skCircle(sketch, "E70", {"center": v(-80.81, 35.39) * mm, "radius": 6.14 * mm});
            skSolve(sketch);
        }
        {
            var Q0;
            Q0=qCreatedBy(makeId("Front.planeOp"),FACE);
            cPlane(context, id + "F54", {"entities" : qUnion([Q0]), "cplaneType" : CPlaneType.OFFSET, "offset" : 35.4 * mm, "oppositeDirection" : true, "width" : 150 * mm, "height" : 150 * mm});
        }
        {
            var Q0;
            Q0=qCreatedBy(id+"F54.planeOp",FACE);
            var sketch = newSketch(context, id + "F55", { "sketchPlane" : qUnion([Q0])});
            skLineSegment(sketch, "E71", {"start": v(-74.68, 10) * mm, "end": v(-80.8, 10) * mm});
            skLineSegment(sketch, "E72", {"start": v(-74.68, 10) * mm, "end": v(-86.95, 10) * mm, "construction": true});
            skLineSegment(sketch, "E73", {"start": v(-80.8, 10) * mm, "end": v(-80.8, 14.33) * mm});
            skArc(sketch, "E74", {"start": v(-74.68, 10) * mm, "mid": v(-77, 13.22) * mm, "end": v(-80.8, 14.33) * mm});
            skSolve(sketch);
        }
        {
            var Q0;
            Q0=qSketchRegion(id+"F55",true);
            var Q1;
            Q1=sQuery(id+"F55.wireOp",EDGE,"E73");
            revolve(context, id + "F56", {"operationType" : NewBodyOperationType.ADD, "entities" : qUnion([Q0]), "axis" : qUnion([Q1]), "revolveType" : RevolveType.FULL});
        }
        {
            var Q0;
            Q0=qCreatedBy(makeId("Top.planeOp"),FACE);
            var sketch = newSketch(context, id + "F57", { "sketchPlane" : qUnion([Q0])});
            skCircle(sketch, "E75", {"center": v(-80.81, -35.39) * mm, "radius": 2 * mm});
            skCircle(sketch, "E76", {"center": v(-80.8, 35.4) * mm, "radius": 6.15 * mm});
            skSolve(sketch);
        }
        {
            var Q0;
            Q0=qSketchRegion(id+"F57",true);
            extrude(context, id + "F58", {"entities" : qUnion([Q0]), "operationType" : NewBodyOperationType.ADD, "depth" : 10 * mm});
        }
        {
            var Q0;
            Q0=makeQuery(id+"F53.imprint","IMPRINT",FACE,{"disambiguationData":[TD([[makeQuery(id+"F53.imprint","IMPRINT",EDGE,{"derivedFrom":sQuery(id+"F53.wireOp",EDGE,"E70")}),1.0]])]});
            var sketch = newSketch(context, id + "F59", { "sketchPlane" : qUnion([Q0])});
            skCircle(sketch, "E77.cCircle", {"center": v(-80.85, 35.39) * mm, "radius": 4 * mm, "construction": true});
            skLineSegment(sketch, "E77.0", {"start": v(-78.5, 39.36) * mm, "end": v(-76.24, 35.34) * mm});
            skLineSegment(sketch, "E77.1", {"start": v(-76.24, 35.34) * mm, "end": v(-78.6, 31.36) * mm});
            skLineSegment(sketch, "E77.2", {"start": v(-78.6, 31.36) * mm, "end": v(-83.2, 31.42) * mm});
            skLineSegment(sketch, "E77.3", {"start": v(-83.2, 31.42) * mm, "end": v(-85.47, 35.44) * mm});
            skLineSegment(sketch, "E77.4", {"start": v(-85.47, 35.44) * mm, "end": v(-83.12, 39.42) * mm});
            skLineSegment(sketch, "E77.5", {"start": v(-83.12, 39.42) * mm, "end": v(-78.5, 39.36) * mm});
            skPoint(sketch, "E77.0.midPoint", {"position": v(-77.37, 37.35) * mm});
            skLineSegment(sketch, "E78", {"start": v(-80.9, 31.4) * mm, "end": v(-80.8, 39.39) * mm, "construction": true});
            skSolve(sketch);
        }
        {
            var Q0;
            Q0=qSketchRegion(id+"F59",true);
            extrude(context, id + "F60", {"entities" : qUnion([Q0]), "operationType" : NewBodyOperationType.REMOVE, "depth" : 4 * mm});
        }
        {
            var Q0;
            Q0=makeQuery(id+"F53.imprint","IMPRINT",FACE,{"disambiguationData":[TD([[makeQuery(id+"F53.imprint","IMPRINT",EDGE,{"derivedFrom":sQuery(id+"F53.wireOp",EDGE,"E70")}),1.0]])]});
            var sketch = newSketch(context, id + "F61", { "sketchPlane" : qUnion([Q0])});
            skCircle(sketch, "E79", {"center": v(-80.8, 35.38) * mm, "radius": 2 * mm});
            skSolve(sketch);
        }
        {
            var Q0;
            Q0=qSketchRegion(id+"F61",true);
            extrude(context, id + "F62", {"entities" : qUnion([Q0]), "operationType" : NewBodyOperationType.REMOVE, "depth" : 7 * mm});
        }
    });
